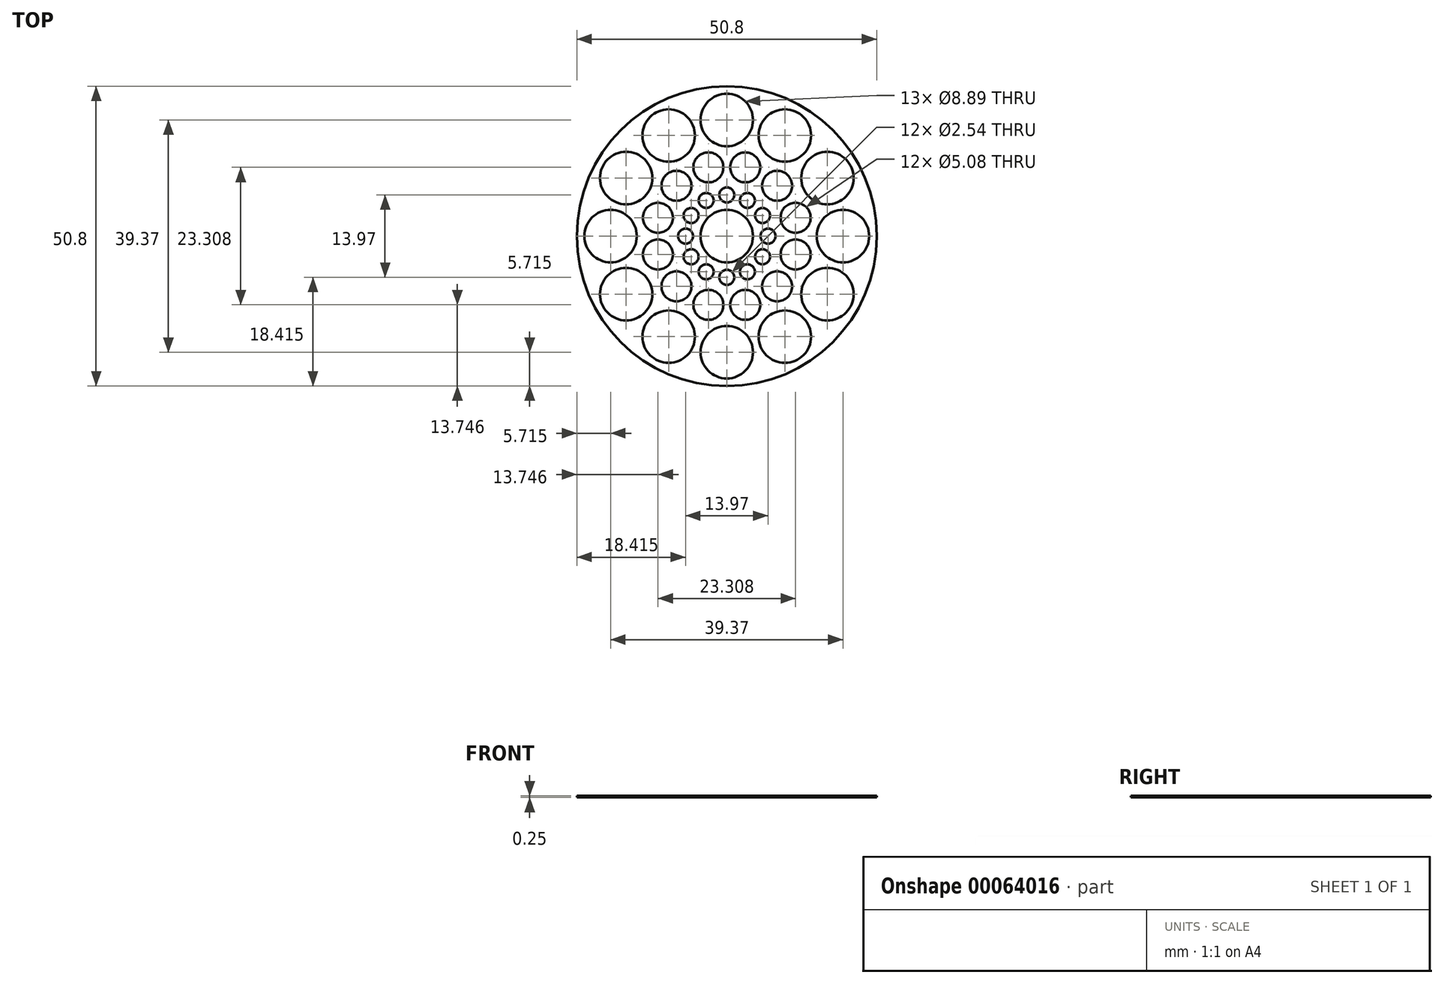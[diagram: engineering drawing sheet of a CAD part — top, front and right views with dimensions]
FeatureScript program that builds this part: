
annotation { "Feature Type Name" : "Feature", "Feature Type Description" : "" }
export const myFeature = defineFeature(function(context is Context, id is Id, definition is map)
    precondition{}
    {
        {
            var Q0;
            Q0=qCreatedBy(makeId("Top.planeOp"),FACE);
            var sketch = newSketch(context, id + "F0", { "sketchPlane" : qUnion([Q0])});
            skCircle(sketch, "E0", {"center": v(0, 0) * mm, "radius": 25.4 * mm});
            skCircle(sketch, "E1", {"center": v(0, 0) * mm, "radius": 19.69 * mm, "construction": true});
            skCircle(sketch, "E2", {"center": v(0, 0) * mm, "radius": 12.07 * mm, "construction": true});
            skCircle(sketch, "E3", {"center": v(0, 0) * mm, "radius": 6.99 * mm, "construction": true});
            skCircle(sketch, "E4", {"center": v(19.69, 0) * mm, "radius": 4.45 * mm});
            skCircle(sketch, "E5", {"center": v(11.65, 3.12) * mm, "radius": 2.54 * mm});
            skLineSegment(sketch, "E6", {"start": v(0, 0) * mm, "end": v(11.65, 3.12) * mm});
            skCircle(sketch, "E7", {"center": v(6.99, 0) * mm, "radius": 1.27 * mm});
            skCircle(sketch, "E8.1.0", {"center": v(6.05, 3.5) * mm, "radius": 1.27 * mm});
            skCircle(sketch, "E8.1.1", {"center": v(17.05, 9.84) * mm, "radius": 4.45 * mm});
            skCircle(sketch, "E8.1.2", {"center": v(8.53, 8.53) * mm, "radius": 2.54 * mm});
            skCircle(sketch, "E8.2.0", {"center": v(3.5, 6.05) * mm, "radius": 1.27 * mm});
            skCircle(sketch, "E8.2.1", {"center": v(9.84, 17.05) * mm, "radius": 4.45 * mm});
            skCircle(sketch, "E8.2.2", {"center": v(3.12, 11.65) * mm, "radius": 2.54 * mm});
            skCircle(sketch, "E8.3.0", {"center": v(0, 6.99) * mm, "radius": 1.27 * mm});
            skCircle(sketch, "E8.3.1", {"center": v(0, 19.69) * mm, "radius": 4.45 * mm});
            skCircle(sketch, "E8.3.2", {"center": v(-3.12, 11.65) * mm, "radius": 2.54 * mm});
            skCircle(sketch, "E8.4.0", {"center": v(-3.5, 6.05) * mm, "radius": 1.27 * mm});
            skCircle(sketch, "E8.4.1", {"center": v(-9.84, 17.05) * mm, "radius": 4.45 * mm});
            skCircle(sketch, "E8.4.2", {"center": v(-8.53, 8.53) * mm, "radius": 2.54 * mm});
            skCircle(sketch, "E8.5.0", {"center": v(-6.05, 3.5) * mm, "radius": 1.27 * mm});
            skCircle(sketch, "E8.5.1", {"center": v(-17.05, 9.84) * mm, "radius": 4.45 * mm});
            skCircle(sketch, "E8.5.2", {"center": v(-11.65, 3.12) * mm, "radius": 2.54 * mm});
            skCircle(sketch, "E9.1.6.0", {"center": v(-6.99, 0) * mm, "radius": 1.27 * mm});
            skCircle(sketch, "E9.2.6.0", {"center": v(-19.69, 0) * mm, "radius": 4.45 * mm});
            skCircle(sketch, "E9.4.6.0", {"center": v(-11.65, -3.12) * mm, "radius": 2.54 * mm});
            skCircle(sketch, "E9.1.7.0", {"center": v(-6.05, -3.5) * mm, "radius": 1.27 * mm});
            skCircle(sketch, "E9.2.7.0", {"center": v(-17.05, -9.84) * mm, "radius": 4.45 * mm});
            skCircle(sketch, "E9.4.7.0", {"center": v(-8.53, -8.53) * mm, "radius": 2.54 * mm});
            skCircle(sketch, "E9.1.8.0", {"center": v(-3.5, -6.05) * mm, "radius": 1.27 * mm});
            skCircle(sketch, "E9.2.8.0", {"center": v(-9.84, -17.05) * mm, "radius": 4.45 * mm});
            skCircle(sketch, "E9.4.8.0", {"center": v(-3.12, -11.65) * mm, "radius": 2.54 * mm});
            skCircle(sketch, "E9.1.9.0", {"center": v(0, -6.99) * mm, "radius": 1.27 * mm});
            skCircle(sketch, "E9.2.9.0", {"center": v(0, -19.69) * mm, "radius": 4.45 * mm});
            skCircle(sketch, "E9.4.9.0", {"center": v(3.12, -11.65) * mm, "radius": 2.54 * mm});
            skCircle(sketch, "E9.1.10.0", {"center": v(3.5, -6.05) * mm, "radius": 1.27 * mm});
            skCircle(sketch, "E9.2.10.0", {"center": v(9.84, -17.05) * mm, "radius": 4.45 * mm});
            skCircle(sketch, "E9.4.10.0", {"center": v(8.53, -8.53) * mm, "radius": 2.54 * mm});
            skCircle(sketch, "E9.1.11.0", {"center": v(6.05, -3.5) * mm, "radius": 1.27 * mm});
            skCircle(sketch, "E9.2.11.0", {"center": v(17.05, -9.84) * mm, "radius": 4.45 * mm});
            skCircle(sketch, "E9.4.11.0", {"center": v(11.65, -3.12) * mm, "radius": 2.54 * mm});
            skCircle(sketch, "E10", {"center": v(0, 0) * mm, "radius": 4.45 * mm});
            skSolve(sketch);
        }
        {
            var Q0;
            Q0 = qSketchRegion(id + "F0", true);
            extrude(context, id + "F1", {"entities" : qUnion([Q0]), "depth" : 0.25 * mm});
        }
    });
